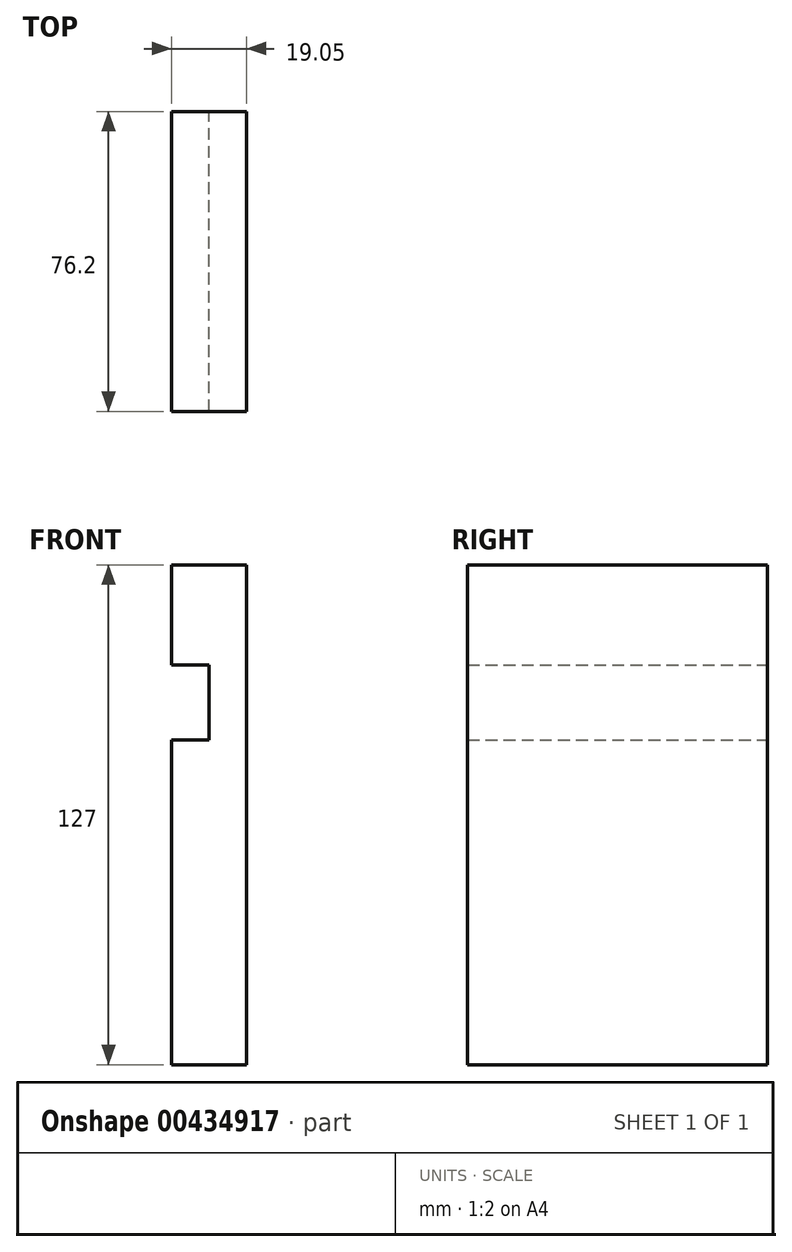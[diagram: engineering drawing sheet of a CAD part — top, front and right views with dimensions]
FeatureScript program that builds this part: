
annotation { "Feature Type Name" : "Feature", "Feature Type Description" : "" }
export const myFeature = defineFeature(function(context is Context, id is Id, definition is map)
    precondition{}
    {
        {
            var Q0;
            Q0=qCreatedBy(makeId("Front.planeOp"),FACE);
            var sketch = newSketch(context, id + "F0", { "sketchPlane" : qUnion([Q0])});
            skLineSegment(sketch, "E0", {"start": v(0, 0) * mm, "end": v(-19.05, 0) * mm});
            skLineSegment(sketch, "E1", {"start": v(0, 0) * mm, "end": v(0, 127) * mm});
            skLineSegment(sketch, "E2", {"start": v(0, 127) * mm, "end": v(-19.05, 127) * mm});
            skLineSegment(sketch, "E3", {"start": v(-19.05, 127) * mm, "end": v(-19.05, 101.6) * mm});
            skLineSegment(sketch, "E4", {"start": v(-19.05, 101.6) * mm, "end": v(-9.52, 101.6) * mm});
            skLineSegment(sketch, "E5", {"start": v(-9.52, 101.6) * mm, "end": v(-9.52, 82.55) * mm});
            skLineSegment(sketch, "E6", {"start": v(-9.52, 82.55) * mm, "end": v(-19.05, 82.55) * mm});
            skLineSegment(sketch, "E7", {"start": v(-19.05, 82.55) * mm, "end": v(-19.05, 0) * mm});
            skSolve(sketch);
        }
        {
            var Q0;
            Q0 = qSketchRegion(id + "F0", true);
            extrude(context, id + "F1", {"entities" : qUnion([Q0]), "depth" : 76.2 * mm});
        }
    });
